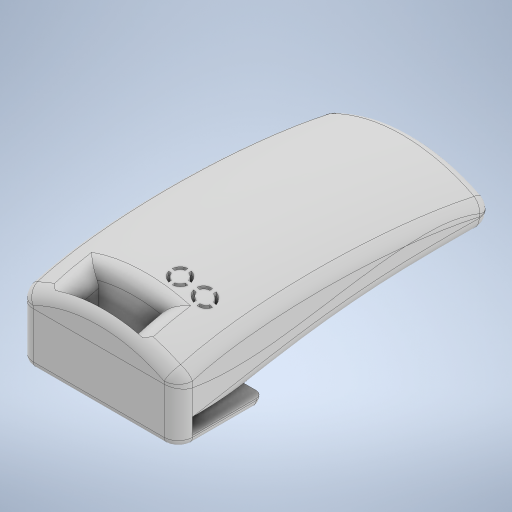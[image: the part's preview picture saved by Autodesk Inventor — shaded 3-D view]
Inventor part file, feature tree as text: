
AUTODESK INVENTOR PART (.ipt)
format: ipt  version: 2023 (Build 270158000, 158)  size: 1,325,056 bytes
history: native  units: mm
features: other x11, sketch x11, extrude x9, fillet x4, plane x2, split x2, shell x2
ambient origin geometry x8: Origin, YZ Plane, XZ Plane, XY Plane, X Axis, Y Axis, Z Axis, Center Point
bodies: Body1 (feature_tree), Body2 (feature_tree), Body3 (feature_tree), Body4 (feature_tree), Body5 (feature_tree)
feature tree (41):
  other  "Sólido1"
  extrude  "Extrusión1"  Depth=45.0mm
  sketch  "Boceto2"  dims[d5=45.0mm d12=4.0mm]
  sketch  "Boceto3"  dims[d13=27.0mm d14=4.0mm d15=4.5mm d16=25.5mm d17=4.5mm]
  fillet  "Empalme1"  Radius=24.0mm
  extrude  "Extrusión2"  Depth=4.0mm
  other  "Empalme de cara2"
  sketch  "Boceto6"  dims[d21=147.5mm d22=0.0mm d23=147.5mm d24=22.5mm d27=17.0mm]
  plane  "Plano de trabajo1"
  extrude  "Extrusión3"  Depth=4.0mm
  sketch  "Boceto8"  dims[d34=17.5mm d35=8.5mm]
  split  "Dividir3"
  fillet  "Empalme2"  Radius=4.5mm
  split  "Dividir4"
  shell  "Vaciado5"  Thickness=25.5mm
  shell  "Vaciado6"  Thickness=4.5mm
  extrude  "Extrusión4"  Depth=67.0mm
  extrude  "Extrusión5"  Depth=147.5mm
  fillet  "Empalme3"  Radius=22.5mm
  fillet  "Empalme4"  Radius=17.0mm
  plane  "Plano de trabajo2"
  other  "Soporte para fiador1"
  sketch  "Boceto14"  dims[d43=53.0mm d44=0.0mm d45=0.0mm d46=4.0mm d51=3.75mm d52=50.25mm d53=0.0mm d54=0.0mm d55=1.0mm d56=1.0mm d57=7.0mm d58=0.0mm d59=2.5mm d60=20.0mm d61=0.0mm d62=2.0mm d63=2.0mm d76=9.0mm d77=60.0mm d78=39.0mm d81=27.0mm d83=24.9mm d84=6.65mm d85=6.95mm d86=34.2mm d87=2.45mm d88=15.5mm d89=0.0mm d90=0.0mm d91=2.95mm d92=1.0mm d93=9.5mm d94=0.0mm d95=0.174533mm d96=40.0mm d98=2.0mm d99=1.5mm d100=3.5mm d101=0.0mm d102=1.745329mm d103=0.436332mm d104=0.0mm d105=0.0mm d106=0.0mm d107=360.0deg d108=0.0mm d109=0.0mm d110=3.5mm d111=1.0mm d112=9.5mm d113=0.349066mm d114=0.174533mm d115=20.0mm d117=2.0mm d118=2.0mm d119=10.0mm d120=0.0mm d121=1.745329mm d122=0.436332mm d123=0.0mm d124=0.0mm d125=0.0mm d126=360.0deg d127=10.0mm d128=0.0mm d129=5.5mm d130=7.0mm d135=6.5mm d136=6.5mm d137=10.0mm d138=0.0mm d139=4.0mm d142=1.0mm d143=0.5mm d144=1.0mm d145=0.5mm d146=1.0mm d147=0.5mm d148=1.0mm d149=0.5mm d150=0.0mm d151=0.0mm d153=8.4mm d154=13.6mm d167=7.0mm d168=0.0mm d169=0.0mm d170=84.5mm d171=1.0mm d131=0.5mm d132=0.872665mm]
  other  "Soporte para fiador2"
  extrude  "Extrusión8"  [1 undecoded]
  extrude  "Extrusión6"  Depth=8.5mm
  extrude  "Extrusión7"  Depth=32.5mm
  extrude  "Extrusión9"  Depth=42.5mm
  sketch  "Boceto1"  dims[d0=89.0mm d1=45.0mm d2=24.0mm d3=0.0mm]
  sketch  "Boceto4"  dims[d18=18.3mm d19=67.0mm]
  sketch  "Boceto7"  dims[d32=4.0mm d33=-1.0mm]
  other  "Sup3"
  sketch  "Boceto9"  dims[d36=1.5mm d37=32.5mm]
  other  "Sup4"
  sketch  "Boceto10"  dims[d38=0.0mm d39=0.0mm d40=42.5mm]
  sketch  "Boceto11"  dims[d41=28.333333mm]
  other  "Sólido4"
  other  "SuperficieBarrido3"
  other  "SuperficieExtrusión1"
  other  "Sólido2"
  other  "Sólido3"
note: 1 required parameter value undecoded (feature->parameter linkage not recoverable at this tier; creation-order binding heuristic only, values carry confidence <= 0.55)
